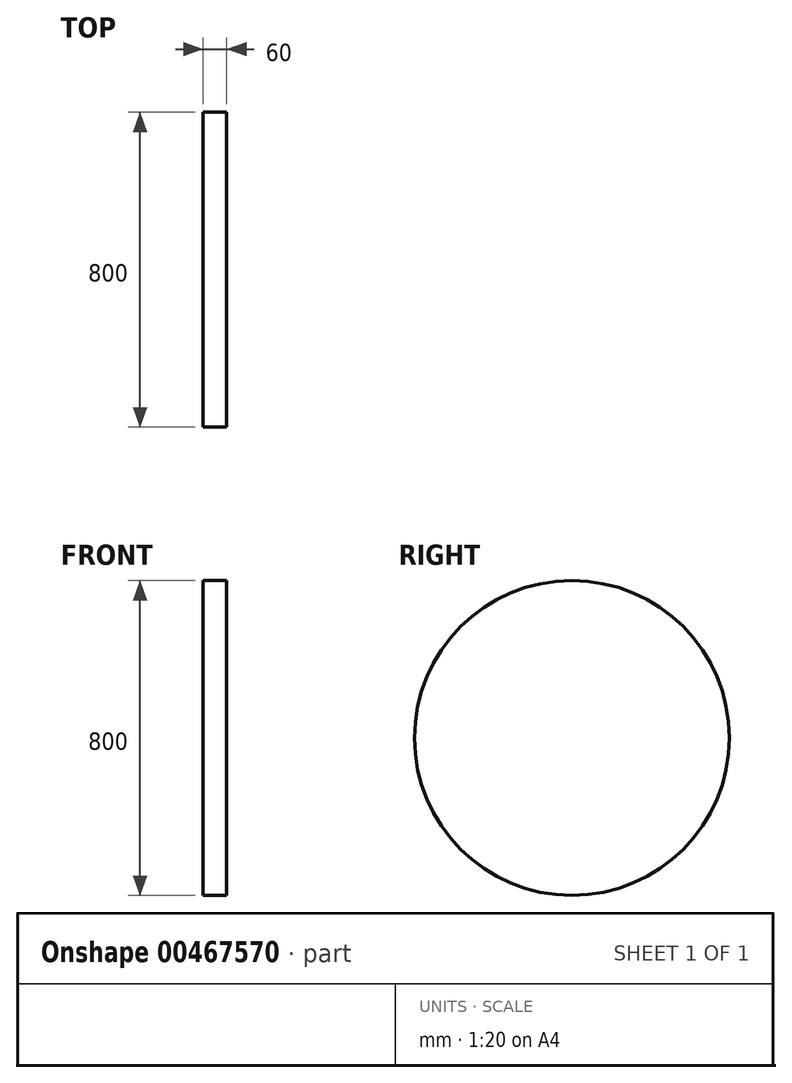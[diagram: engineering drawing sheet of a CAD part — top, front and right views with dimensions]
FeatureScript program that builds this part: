
annotation { "Feature Type Name" : "Feature", "Feature Type Description" : "" }
export const myFeature = defineFeature(function(context is Context, id is Id, definition is map)
    precondition{}
    {
        {
            var Q0;
            Q0=qCreatedBy(makeId("Right.planeOp"),FACE);
            var sketch = newSketch(context, id + "F0", { "sketchPlane" : qUnion([Q0])});
            skCircle(sketch, "E0", {"center": v(0, 0) * mm, "radius": 400 * mm});
            skSolve(sketch);
        }
        {
            var Q0;
            Q0=makeQuery(id+"F0.imprint","IMPRINT",FACE,{"disambiguationData":[TD([[makeQuery(id+"F0.imprint","IMPRINT",EDGE,{"derivedFrom":sQuery(id+"F0.wireOp",EDGE,"E0")}),1.0]])]});
            extrude(context, id + "F1", {"entities" : qUnion([Q0]), "depth" : 60 * mm});
        }
    });
